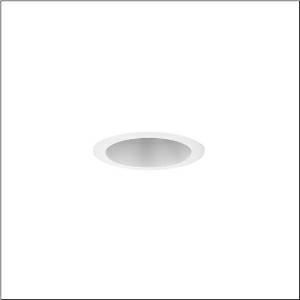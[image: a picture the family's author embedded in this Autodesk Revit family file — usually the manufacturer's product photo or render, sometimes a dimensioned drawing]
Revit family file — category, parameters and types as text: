
# Revit family: lunis_31-l_51dn16me31b
name_source: partatom
category: Lighting Fixtures
units: mm (PartAtom-declared; Revit-internal decimal feet)

## family parameters
Cut with Voids When Loaded = No
Host = Face
Light Source = No
Part Type = Normal
Room Calculation Point = No
Round Connector Dimension = Use Diameter
Shared = No

## types (1)
- --- (1 x LED, 1600 lm, 11.5 W, 3000K)
    Apparent Load = 12 VA
    CIE Flux Codes = 76 93 99 100 100
    Color Rendering = 80
    Color Temperature = 3000K
    Default Elevation = 1800 mm
    Description = Lunis 31-L, downlight, light control with reflector, light emission: direct distribution, LED rated luminous flux: 1.600lm, light colour: 830, mains connection: 220..240V, AC/DC, 0/50..60Hz, housing, of aluminium, white, protection rating (complete): IP20, protection rating (on room side): IP54, insulation class (complete): insulation class II (safety insulation), certification: CE, ENEC, packaging unit: 1 piece
    Height = 0 mm  [stored 0 ft]
    Lamp = 1 x LED
    Lamp Light Flux = 1600 lm
    Lamp Power = 11.5 W
    Lamp count = 1
    Length = 188 mm
    Luminous efficacy = 139 lm/W
    Manufacturer = Siteco
    ModVariant = No
    Model = 51DN16ME31B
    Mounting Place = Ceiling
    Mounting Type = Recessed
    Number of Poles = 1
    OnlyDefault = Yes
    Power Factor = 1
    Product Name = Lunis 31-L
    Product group = downlight
    ProductGroupID = 401
    Protection Class = Protection class II
    Protection Degree = IP 20
    RLX_Detail_Level = 1
    RLX_Emergency_Light_Flux = 0 lm
    RLX_Emergency_Type = 0
    RLX_Emergency_Type_DB = No
    RlxData = <blob elided: 22417 chars, md5=e80358f7>
    Socket = socket
    Standby Power = 0 W
    System Light Flux = 1600 lm
    System Power = 12 W
    Type Comments = individual setting: luminous flux: 100 % | (OFF | ON) | 300 mA
    Type Image = l_1345911.jpg
    URL = http://relux.com
    VarID = @adj_029897
    Voltage = 0 V
    Weight = 0.00 kg
    Width = 0 mm  [stored 0 ft]

note: [stored X ft] marks values corroborated as IEEE doubles in the binary element streams (Revit-internal decimal feet)

## geometry (parser evidence)
native form markers: Blend x4, Sweep x10
no freeform markers — native parametric forms only
